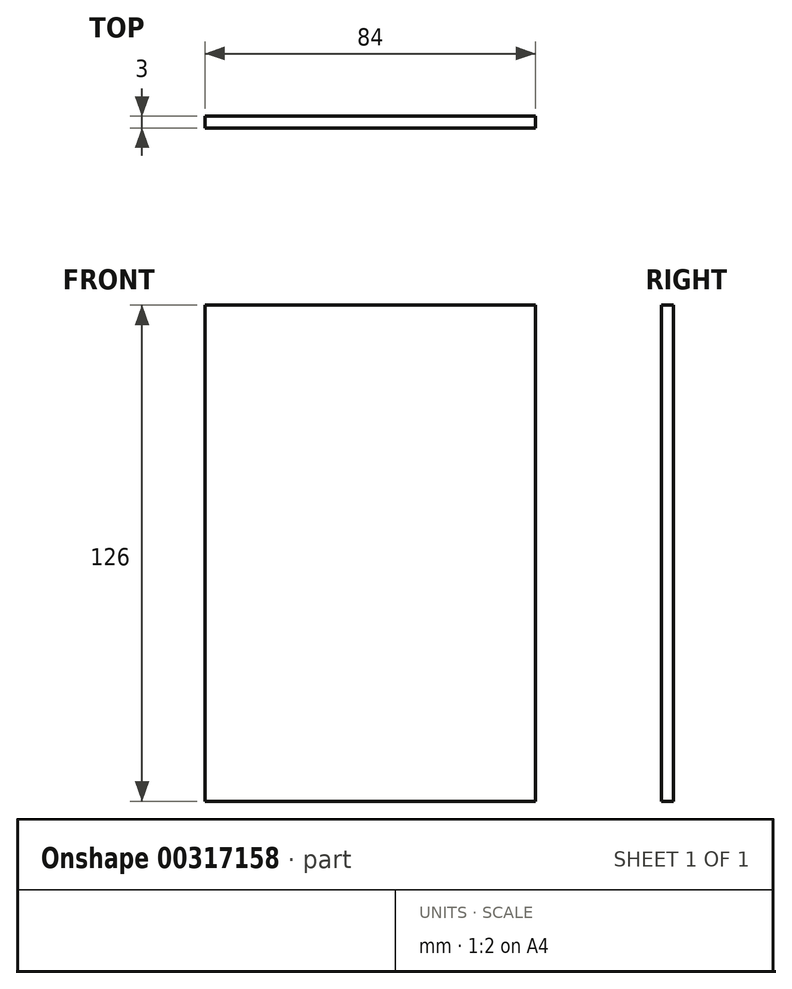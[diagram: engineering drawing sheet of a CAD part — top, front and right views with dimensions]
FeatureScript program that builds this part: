
annotation { "Feature Type Name" : "Feature", "Feature Type Description" : "" }
export const myFeature = defineFeature(function(context is Context, id is Id, definition is map)
    precondition{}
    {
        {
            var Q0;
            Q0=qCreatedBy(makeId("Front.planeOp"),FACE);
            var sketch = newSketch(context, id + "F0", { "sketchPlane" : qUnion([Q0])});
            skLineSegment(sketch, "E0.bottom", {"start": v(42, 63) * mm, "end": v(-42, 63) * mm});
            skLineSegment(sketch, "E0.top", {"start": v(42, -63) * mm, "end": v(-42, -63) * mm});
            skLineSegment(sketch, "E0.left", {"start": v(42, 63) * mm, "end": v(42, -63) * mm});
            skLineSegment(sketch, "E0.right", {"start": v(-42, 63) * mm, "end": v(-42, -63) * mm});
            skPoint(sketch, "E0.middle", {"position": v(0, 0) * mm});
            skSolve(sketch);
        }
        {
            var Q0;
            Q0=qSketchRegion(id+"F0",true);
            extrude(context, id + "F1", {"entities" : qUnion([Q0]), "depth" : 3 * mm});
        }
    });
